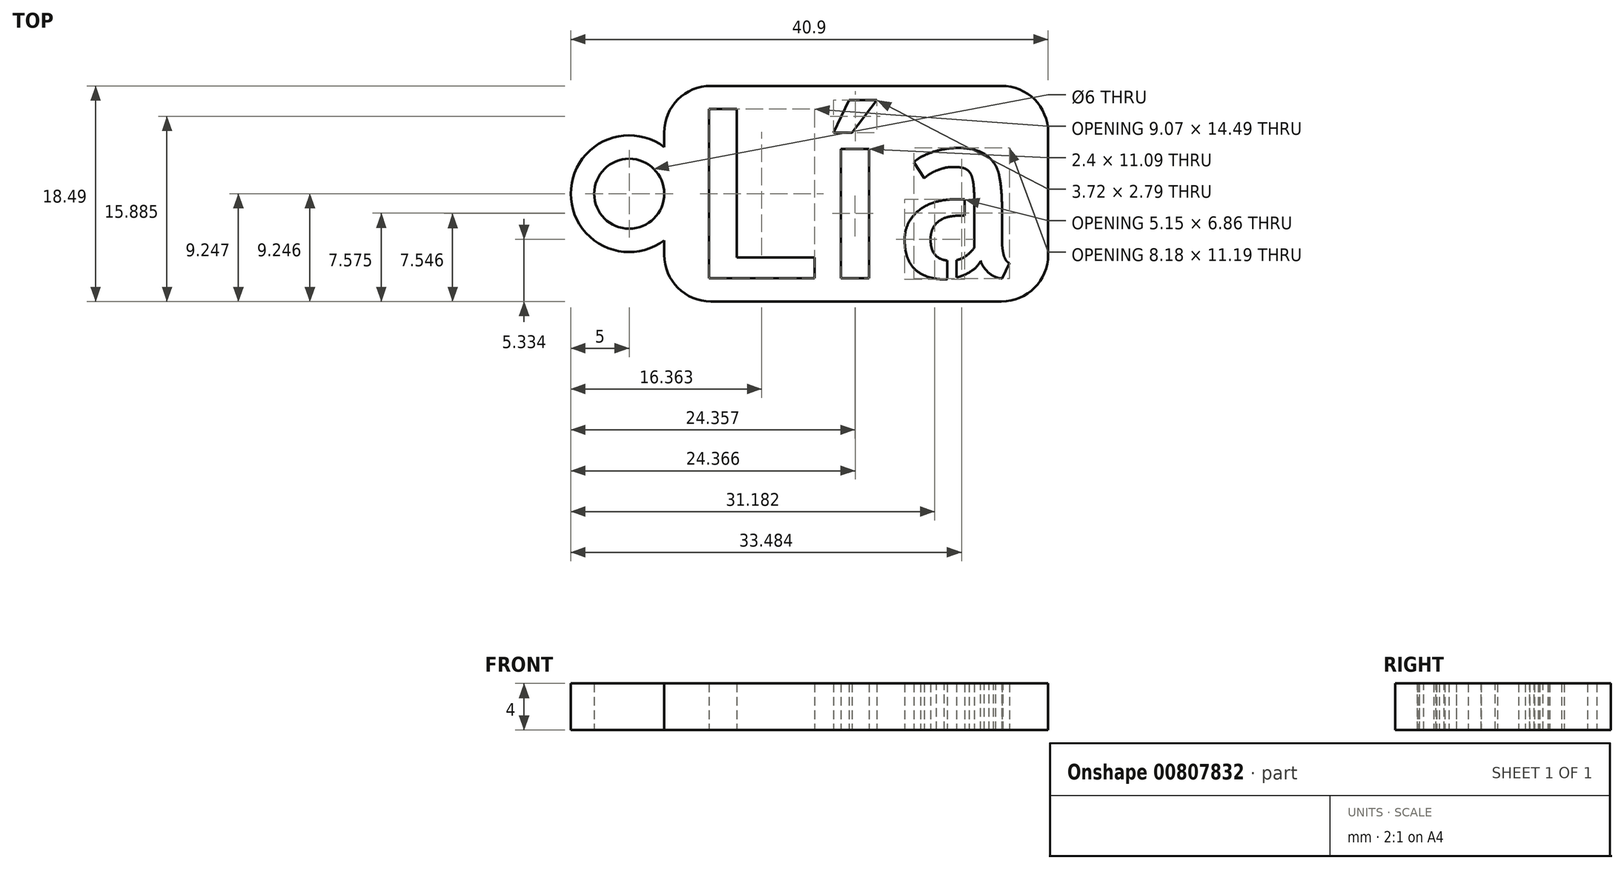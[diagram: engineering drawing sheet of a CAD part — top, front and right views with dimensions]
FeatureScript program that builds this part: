
annotation { "Feature Type Name" : "Feature", "Feature Type Description" : "" }
export const myFeature = defineFeature(function(context is Context, id is Id, definition is map)
    precondition{}
    {
        {
            var Q0;
            Q0=qCreatedBy(makeId("Top.planeOp"),FACE);
            var sketch = newSketch(context, id + "F0", { "sketchPlane" : qUnion([Q0])});
            skLineSegment(sketch, "E0.bottom", {"start": v(-2, -2) * mm, "end": v(30.9, -2) * mm});
            skLineSegment(sketch, "E0.top", {"start": v(-2, 16.5) * mm, "end": v(30.9, 16.5) * mm});
            skLineSegment(sketch, "E0.left", {"start": v(-2, -2) * mm, "end": v(-2, 3.25) * mm});
            skLineSegment(sketch, "E0.right", {"start": v(30.9, -2) * mm, "end": v(30.9, 16.5) * mm});
            skArc(sketch, "E1", {"start": v(-2, 11.25) * mm, "mid": v(-10, 7.25) * mm, "end": v(-2, 3.25) * mm});
            skLineSegment(sketch, "E2.trimOffspring", {"start": v(-2, 11.25) * mm, "end": v(-2, 16.5) * mm});
            skCircle(sketch, "E3", {"center": v(-5, 7.25) * mm, "radius": 3 * mm});
            skLineSegment(sketch, "E4", {"start": v(30.9, 7.25) * mm, "end": v(-10, 7.25) * mm, "construction": true});
            skText(sketch, "E5", { "text": "Lía", "fontName": "AllertaStencil-Regular.ttf"});
            const initialGuessF0  = {"E5": [0, 0, 1, 0, 0.0145]};
            skSetInitialGuess(sketch, initialGuessF0);
            skSolve(sketch);
        }
        {
            var Q0;
            Q0=makeQuery(id+"F0.imprint","IMPRINT",FACE,{"disambiguationData":[TD([[makeQuery(id+"F0.imprint","IMPRINT",EDGE,{"derivedFrom":sQuery(id+"F0.wireOp",EDGE,"E0.bottom")}),1.0]])]});
            extrude(context, id + "F1", {"entities" : qUnion([Q0]), "depth" : 4 * mm, "offsetDistance" : 25 * mm});
        }
        {
            var Q0;
            Q0=makeQuery(id+"F1.opExtrude","SWEPT_EDGE",EDGE,{"disambiguationData":[OSD([sQuery(id+"F0.wireOp",EDGE,"E0.bottom"),sQuery(id+"F0.wireOp",EDGE,"E0.left")])]});
            var Q1;
            Q1=makeQuery(id+"F1.opExtrude","SWEPT_EDGE",EDGE,{"disambiguationData":[OSD([sQuery(id+"F0.wireOp",EDGE,"E0.bottom"),sQuery(id+"F0.wireOp",EDGE,"E0.right")])]});
            var Q2;
            Q2=makeQuery(id+"F1.opExtrude","SWEPT_EDGE",EDGE,{"disambiguationData":[OSD([sQuery(id+"F0.wireOp",EDGE,"E0.top"),sQuery(id+"F0.wireOp",EDGE,"E0.right")])]});
            var Q3;
            Q3=makeQuery(id+"F1.opExtrude","SWEPT_EDGE",EDGE,{"disambiguationData":[OSD([sQuery(id+"F0.wireOp",EDGE,"E0.top"),sQuery(id+"F0.wireOp",EDGE,"E2.trimOffspring")])]});
            fillet(context, id + "F2", {"entities" : qUnion([Q0, Q1, Q2, Q3]), "radius" : 4 * mm, "tangentPropagation" : true, "allowEdgeOverflow" : false});
        }
    });
